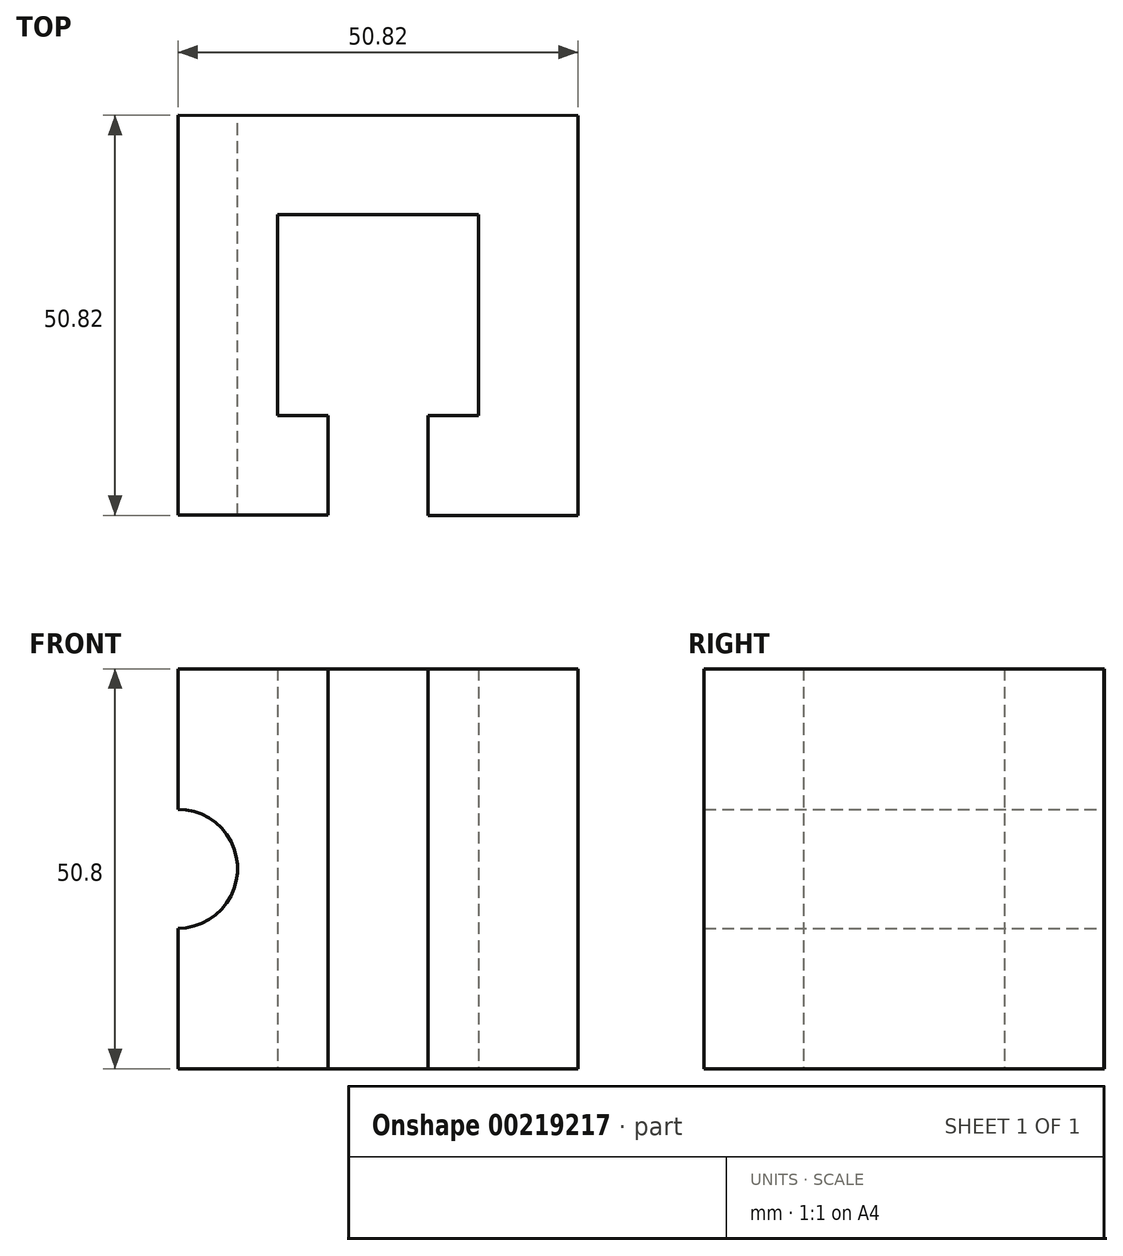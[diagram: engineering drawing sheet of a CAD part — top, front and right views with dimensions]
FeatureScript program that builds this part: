
annotation { "Feature Type Name" : "Feature", "Feature Type Description" : "" }
export const myFeature = defineFeature(function(context is Context, id is Id, definition is map)
    precondition{}
    {
        {
            var Q0;
            Q0=qCreatedBy(makeId("Top.planeOp"),FACE);
            var sketch = newSketch(context, id + "F0", { "sketchPlane" : qUnion([Q0])});
            skLineSegment(sketch, "E0.bottom", {"start": v(25.41, 25.39) * mm, "end": v(-25.39, 25.41) * mm});
            skLineSegment(sketch, "E0.left", {"start": v(25.41, 25.39) * mm, "end": v(25.39, -25.41) * mm});
            skLineSegment(sketch, "E0.right", {"start": v(-25.39, 25.41) * mm, "end": v(-25.41, -25.39) * mm});
            skPoint(sketch, "E0.middle", {"position": v(0, 0) * mm});
            skLineSegment(sketch, "E1.bottom", {"start": v(12.76, 12.76) * mm, "end": v(-12.76, 12.76) * mm});
            skLineSegment(sketch, "E1.left", {"start": v(12.76, 12.76) * mm, "end": v(12.76, -12.76) * mm});
            skLineSegment(sketch, "E1.right", {"start": v(-12.76, 12.76) * mm, "end": v(-12.76, -12.76) * mm});
            skLineSegment(sketch, "E2", {"start": v(6.36, -12.76) * mm, "end": v(6.36, -25.41) * mm});
            skLineSegment(sketch, "E3", {"start": v(6.36, -12.76) * mm, "end": v(12.76, -12.76) * mm});
            skLineSegment(sketch, "E4", {"start": v(-6.34, -12.76) * mm, "end": v(-12.76, -12.76) * mm});
            skLineSegment(sketch, "E5", {"start": v(-6.34, -12.76) * mm, "end": v(-6.34, -25.39) * mm});
            skLineSegment(sketch, "E6", {"start": v(-25.41, -25.39) * mm, "end": v(-6.34, -25.39) * mm});
            skLineSegment(sketch, "E7", {"start": v(6.36, -25.41) * mm, "end": v(25.39, -25.41) * mm});
            skSolve(sketch);
        }
        {
            var Q0;
            Q0=makeQuery(id+"F0.imprint","IMPRINT",FACE,{"disambiguationData":[TD([[makeQuery(id+"F0.imprint","IMPRINT",EDGE,{"derivedFrom":sQuery(id+"F0.wireOp",EDGE,"E0.bottom")}),1.0]])]});
            extrude(context, id + "F1", {"entities" : qUnion([Q0]), "depth" : 50.8 * mm});
        }
        {
            var Q0;
            Q0=makeQuery(id+"F1.opExtrude","SWEPT_FACE",FACE,{"disambiguationData":[OSD([sQuery(id+"F0.wireOp",EDGE,"E0.bottom")])]});
            var sketch = newSketch(context, id + "F2", { "sketchPlane" : qUnion([Q0])});
            skPoint(sketch, "E8", {"position": v(25.4, 25.4) * mm});
            skCircle(sketch, "E9", {"center": v(25.4, 25.4) * mm, "radius": 7.56 * mm});
            skSolve(sketch);
        }
        {
            var Q0;
            {var subQ0=sQuery(id+"F2.wireOp",EDGE,"E9");var subQ1=makeQuery(id+"F1.opExtrude","SWEPT_EDGE",EDGE,{"disambiguationData":[OSD([sQuery(id+"F0.wireOp",EDGE,"E0.bottom"),sQuery(id+"F0.wireOp",EDGE,"E0.right")])]});var subQ2=makeQuery(id+"F2.imprint","INTERSECT",VERTEX,{"disambiguationData":[OD(0.0)],"derivedFrom":[subQ1,subQ0]});Q0=makeQuery(id+"F2.imprint","IMPRINT",FACE,{"disambiguationData":[TD([[makeQuery(id+"F2.imprint","IMPRINT",EDGE,{"disambiguationData":[TD([[subQ2,1.0]])],"derivedFrom":subQ0}),1.0]])]});}
            extrude(context, id + "F3", {"entities" : qUnion([Q0]), "operationType" : NewBodyOperationType.REMOVE, "oppositeDirection" : true, "depth" : 57.15 * mm});
        }
    });
